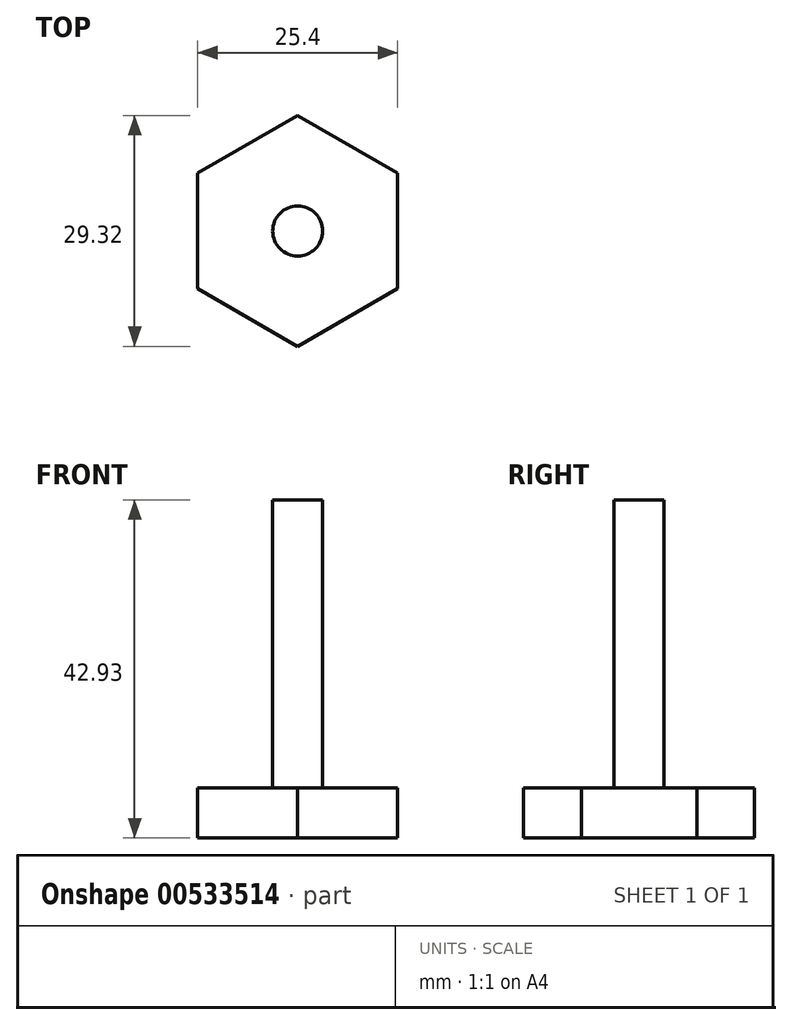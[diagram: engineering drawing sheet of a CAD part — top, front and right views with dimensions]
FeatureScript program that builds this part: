
annotation { "Feature Type Name" : "Feature", "Feature Type Description" : "" }
export const myFeature = defineFeature(function(context is Context, id is Id, definition is map)
    precondition{}
    {
        {
            var Q0;
            Q0=qCreatedBy(makeId("Top.planeOp"),FACE);
            var sketch = newSketch(context, id + "F0", { "sketchPlane" : qUnion([Q0])});
            skCircle(sketch, "E0.cCircle", {"center": v(0, 0) * mm, "radius": 12.7 * mm, "construction": true});
            skLineSegment(sketch, "E0.0", {"start": v(-12.7, -7.33) * mm, "end": v(-12.7, 7.33) * mm});
            skLineSegment(sketch, "E0.1", {"start": v(-12.7, 7.33) * mm, "end": v(0, 14.66) * mm});
            skLineSegment(sketch, "E0.2", {"start": v(0, 14.66) * mm, "end": v(12.7, 7.33) * mm});
            skLineSegment(sketch, "E0.3", {"start": v(12.7, 7.33) * mm, "end": v(12.7, -7.33) * mm});
            skLineSegment(sketch, "E0.4", {"start": v(12.7, -7.33) * mm, "end": v(0, -14.66) * mm});
            skLineSegment(sketch, "E0.5", {"start": v(0, -14.66) * mm, "end": v(-12.7, -7.33) * mm});
            skPoint(sketch, "E0.0.midPoint", {"position": v(-12.7, 0) * mm});
            skSolve(sketch);
        }
        {
            var Q0;
            Q0=makeQuery(id+"F0.imprint","IMPRINT",FACE,{"disambiguationData":[TD([[makeQuery(id+"F0.imprint","IMPRINT",EDGE,{"derivedFrom":sQuery(id+"F0.wireOp",EDGE,"E0.0")}),-1.0]])]});
            extrude(context, id + "F1", {"entities" : qUnion([Q0]), "flatOperationType" : FlatOperationType.REMOVE, "depth" : 6.35 * mm, "offsetDistance" : 25.4 * mm, "domain" : OperationDomain.MODEL});
        }
        {
            var Q0;
            Q0=makeQuery(id+"F1.opExtrude","CAP_FACE",FACE,{"disambiguationData":[OSD([sQuery(id+"F0.wireOp",EDGE,"E0.0"),sQuery(id+"F0.wireOp",EDGE,"E0.1"),sQuery(id+"F0.wireOp",EDGE,"E0.2"),sQuery(id+"F0.wireOp",EDGE,"E0.3"),sQuery(id+"F0.wireOp",EDGE,"E0.4"),sQuery(id+"F0.wireOp",EDGE,"E0.5")])],"isStart":false});
            var sketch = newSketch(context, id + "F2", { "sketchPlane" : qUnion([Q0])});
            skCircle(sketch, "E1", {"center": v(0, 0) * mm, "radius": 3.18 * mm});
            skSolve(sketch);
        }
        {
            var Q0;
            Q0 = qSketchRegion(id + "F2", true);
            extrude(context, id + "F3", {"entities" : qUnion([Q0]), "operationType" : NewBodyOperationType.ADD, "depth" : 36.58 * mm, "offsetDistance" : 25.4 * mm});
        }
    });
